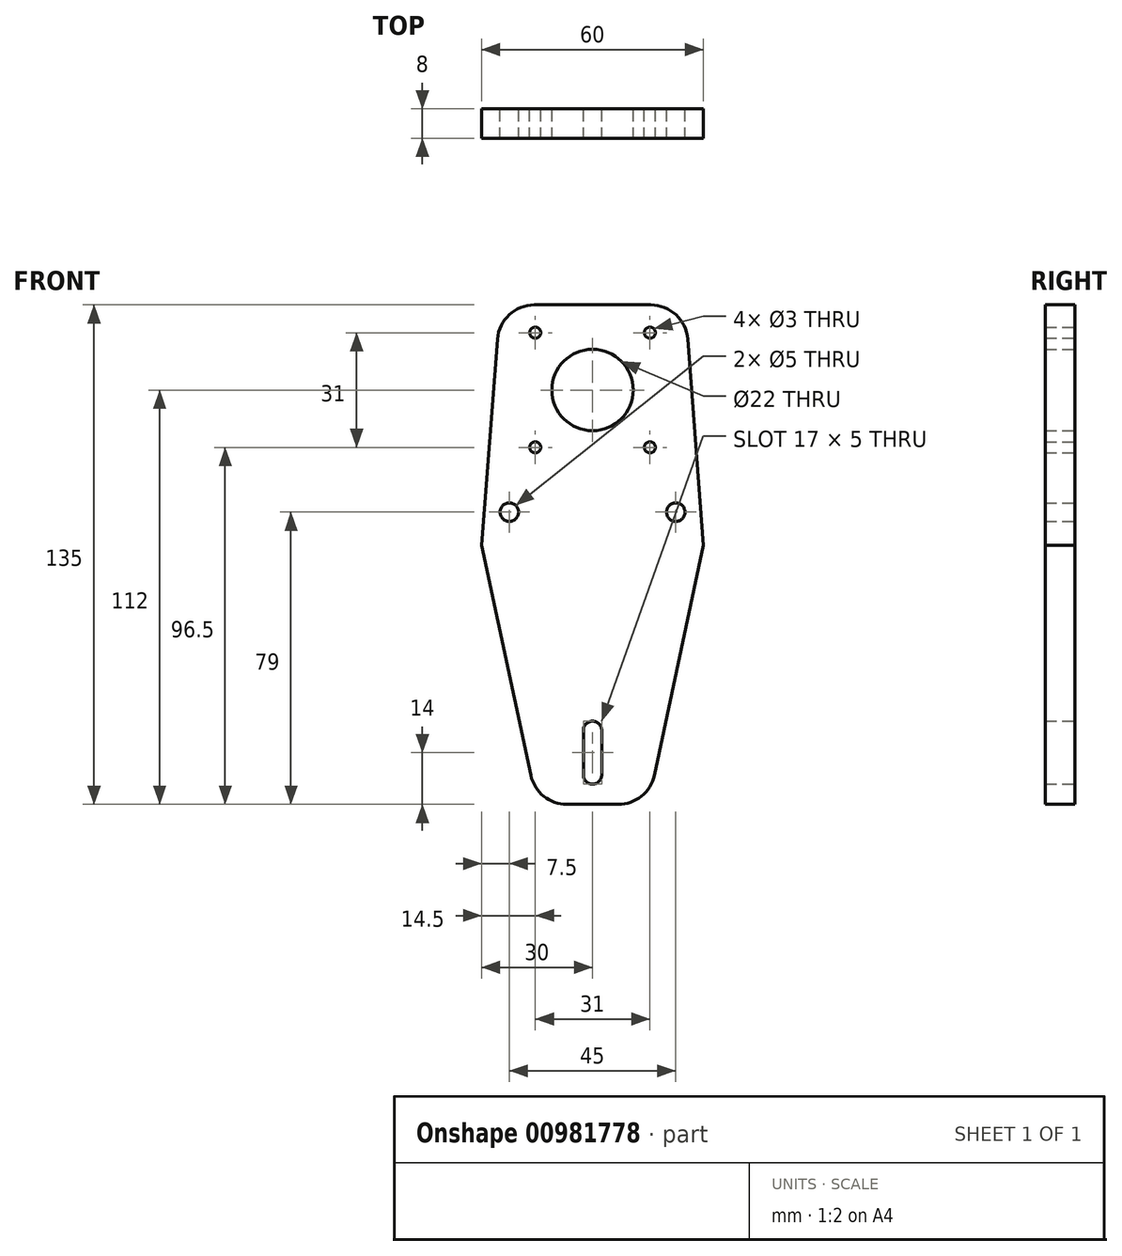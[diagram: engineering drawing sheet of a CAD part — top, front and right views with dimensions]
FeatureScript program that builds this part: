
annotation { "Feature Type Name" : "Feature", "Feature Type Description" : "" }
export const myFeature = defineFeature(function(context is Context, id is Id, definition is map)
    precondition{}
    {
        {
            var Q0;
            Q0=qCreatedBy(makeId("Front.planeOp"),FACE);
            var sketch = newSketch(context, id + "F0", { "sketchPlane" : qUnion([Q0])});
            skPoint(sketch, "E0.middle", {"position": v(0, 0) * mm});
            skPoint(sketch, "E1.centerSnap0", {"position": v(0, -70) * mm});
            skLineSegment(sketch, "E2", {"start": v(-2.5, -50) * mm, "end": v(-2.5, -62) * mm});
            skLineSegment(sketch, "E3", {"start": v(2.5, -50) * mm, "end": v(2.5, -62) * mm});
            skArc(sketch, "E4", {"start": v(-2.5, -62) * mm, "mid": v(0, -64.5) * mm, "end": v(2.5, -62) * mm});
            skCircle(sketch, "E5", {"center": v(0, 42) * mm, "radius": 11 * mm});
            skCircle(sketch, "E6", {"center": v(-15.5, 57.5) * mm, "radius": 1.5 * mm});
            skCircle(sketch, "E7", {"center": v(15.5, 57.5) * mm, "radius": 1.5 * mm});
            skCircle(sketch, "E8", {"center": v(15.5, 26.5) * mm, "radius": 1.5 * mm});
            skCircle(sketch, "E9", {"center": v(-15.5, 26.5) * mm, "radius": 1.5 * mm});
            skArc(sketch, "E10", {"start": v(2.5, -50) * mm, "mid": v(0, -47.5) * mm, "end": v(-2.5, -50) * mm});
            skCircle(sketch, "E11", {"center": v(22.5, 9) * mm, "radius": 2.5 * mm});
            skCircle(sketch, "E12", {"center": v(-22.5, 9) * mm, "radius": 2.5 * mm});
            skLineSegment(sketch, "E13", {"start": v(0, 0) * mm, "end": v(30, 0) * mm, "construction": true});
            skLineSegment(sketch, "E14", {"start": v(0, 0) * mm, "end": v(-30, 0) * mm, "construction": true});
            skLineSegment(sketch, "E15", {"start": v(0, 65) * mm, "end": v(-15.74, 65) * mm});
            skLineSegment(sketch, "E16", {"start": v(-25.71, 55.77) * mm, "end": v(-30, 0) * mm});
            skLineSegment(sketch, "E17.MirrorCS", {"start": v(25.71, 55.77) * mm, "end": v(30, 0) * mm});
            skLineSegment(sketch, "E18.MirrorCS", {"start": v(0, 65) * mm, "end": v(15.74, 65) * mm});
            skPoint(sketch, "E19.visualSharp", {"position": v(-25, 65) * mm});
            skArc(sketch, "E19.filletArc", {"start": v(-15.74, 65) * mm, "mid": v(-22.53, 62.34) * mm, "end": v(-25.71, 55.77) * mm});
            skPoint(sketch, "E20.visualSharp", {"position": v(25, 65) * mm});
            skArc(sketch, "E20.filletArc", {"start": v(25.71, 55.77) * mm, "mid": v(22.53, 62.34) * mm, "end": v(15.74, 65) * mm});
            skLineSegment(sketch, "E21", {"start": v(0, -70) * mm, "end": v(-6.92, -70) * mm});
            skLineSegment(sketch, "E22", {"start": v(0, -70) * mm, "end": v(6.92, -70) * mm});
            skLineSegment(sketch, "E23", {"start": v(16.7, -62.1) * mm, "end": v(30, 0) * mm});
            skLineSegment(sketch, "E24", {"start": v(-16.7, -62.1) * mm, "end": v(-30, 0) * mm});
            skPoint(sketch, "E25.visualSharp", {"position": v(-15, -70) * mm});
            skArc(sketch, "E25.filletArc", {"start": v(-16.7, -62.1) * mm, "mid": v(-13.2, -67.78) * mm, "end": v(-6.92, -70) * mm});
            skPoint(sketch, "E26.visualSharp", {"position": v(15, -70) * mm});
            skArc(sketch, "E26.filletArc", {"start": v(6.92, -70) * mm, "mid": v(13.2, -67.78) * mm, "end": v(16.7, -62.1) * mm});
            skSolve(sketch);
        }
        {
            assignVariable(context, id + "F1", {"name" : "Plexiglas", "anyValue" : 8});
        }
        {
            var Q0;
            Q0=makeQuery(id+"F0.imprint","IMPRINT",FACE,{"disambiguationData":[TD([[makeQuery(id+"F0.imprint","IMPRINT",EDGE,{"derivedFrom":sQuery(id+"F0.wireOp",EDGE,"E2")}),-1.0]])]});
            extrude(context, id + "F2", {"entities" : qUnion([Q0]), "depth" : (getVariable(context, 'Plexiglas')) * mm, "offsetDistance" : 25 * mm});
        }
    });
